# Revit family: 1286098 Ascoli Twin Recessed
name_source: partatom
category: Lighting Fixtures
revit_build: Autodesk Revit 2018 (Build: 20170223_1515(x64)
units: mm (PartAtom-declared; Revit-internal decimal feet)

## family parameters
Always vertical = Yes
Cut with Voids When Loaded = No
Host = Ceiling
Light Source = No
OmniClass Number = 23.80.70.11
OmniClass Title = Luminaries for Internal Lighting
Part Type = Normal
Room Calculation Point = No
Round Connector Dimension = Use Diameter
Shared = No

## types (2) — shared parameters
Manufacturer URL - Europe and Rest of World = www.astrolighting.com
Manufacturer URL - North America = us.astrolighting.com
Product CCT = 2700K / 3000K

## per-type parameters (varying)
| type | ADA compliant | Dimmable | Dimming Method | Driver Included | Driver Required | Efficacy (lm/w) | Electrical Class | Lamp | Light Source Fixed | Location / IP Rating | Main Finish | Main Material | Power (Watts) | Product CRI | Product Dimensions (MM) | Product Location | Product Name | Product SKU | Product URL | Product Weight (KG) |
| CE | Not Applicable | Yes | Lamp Dependant | Not Applicable | Not Applicable | Lamp Dependant | 1 | 2 x Halogen - 50W Max - MR16 GU10 | Yes | IP20 | Bronze | Metal - Mild Steel | 50W Max | 80 / 90 | 120 x 295 x 21 | Architectural Indoor | Ascoli Twin Recessed | 1285098 | https://www.astrolighting.com | 1 mm  [stored 0.00328084 ft] |
| ETL |  |  |  |  |  |  |  |  |  |  |  |  |  | 80/ 90 |  |  |  | 1234567 |  | 0 mm  [stored 0 ft] |

note: [stored X ft] marks values corroborated as IEEE doubles in the binary element streams (Revit-internal decimal feet)

## geometry (parser evidence)
native form markers: Sweep x2
no freeform markers — native parametric forms only
